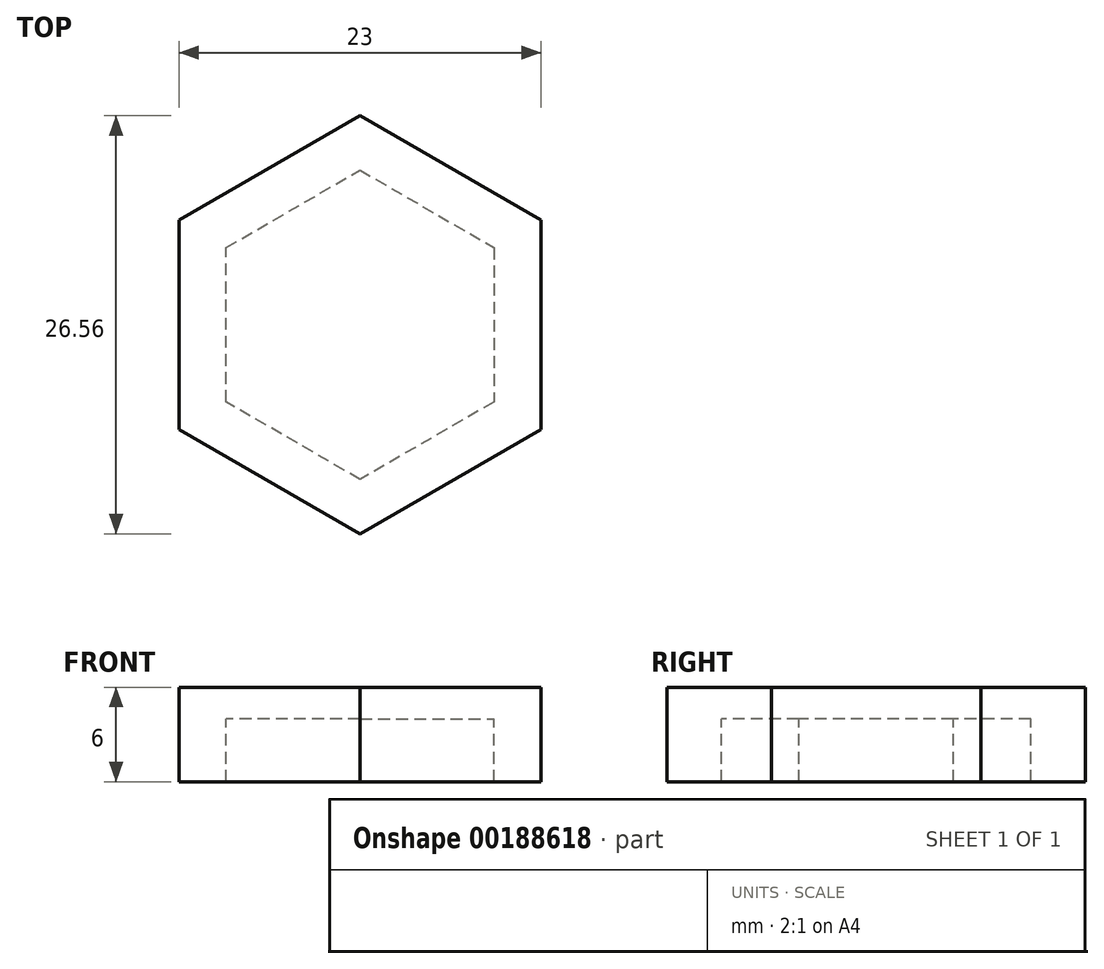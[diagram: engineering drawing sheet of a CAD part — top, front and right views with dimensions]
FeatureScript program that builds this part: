
annotation { "Feature Type Name" : "Feature", "Feature Type Description" : "" }
export const myFeature = defineFeature(function(context is Context, id is Id, definition is map)
    precondition{}
    {
        {
            var Q0;
            Q0=qCreatedBy(makeId("Top.planeOp"),FACE);
            var sketch = newSketch(context, id + "F0", { "sketchPlane" : qUnion([Q0])});
            skCircle(sketch, "E0.cCircle", {"center": v(0, 0) * mm, "radius": 8.5 * mm, "construction": true});
            skLineSegment(sketch, "E0.0", {"start": v(8.5, 4.9) * mm, "end": v(8.5, -4.9) * mm});
            skLineSegment(sketch, "E0.1", {"start": v(8.5, -4.9) * mm, "end": v(0, -9.81) * mm});
            skLineSegment(sketch, "E0.2", {"start": v(0, -9.81) * mm, "end": v(-8.5, -4.9) * mm});
            skLineSegment(sketch, "E0.3", {"start": v(-8.5, -4.9) * mm, "end": v(-8.5, 4.9) * mm});
            skLineSegment(sketch, "E0.4", {"start": v(-8.5, 4.9) * mm, "end": v(0, 9.81) * mm});
            skLineSegment(sketch, "E0.5", {"start": v(0, 9.81) * mm, "end": v(8.5, 4.9) * mm});
            skPoint(sketch, "E0.0.midPoint", {"position": v(8.5, 0) * mm});
            skLineSegment(sketch, "E1.0", {"start": v(0, 13.28) * mm, "end": v(11.5, 6.64) * mm});
            skLineSegment(sketch, "E1.1", {"start": v(11.5, -6.64) * mm, "end": v(0, -13.28) * mm});
            skLineSegment(sketch, "E1.2", {"start": v(0, -13.28) * mm, "end": v(-11.5, -6.64) * mm});
            skLineSegment(sketch, "E1.3", {"start": v(11.5, 6.64) * mm, "end": v(11.5, -6.64) * mm});
            skLineSegment(sketch, "E1.4", {"start": v(-11.5, -6.64) * mm, "end": v(-11.5, 6.64) * mm});
            skLineSegment(sketch, "E1.5", {"start": v(-11.5, 6.64) * mm, "end": v(0, 13.28) * mm});
            skSolve(sketch);
        }
        {
            var Q0;
            Q0=makeQuery(id+"F0.imprint","IMPRINT",FACE,{"disambiguationData":[TD([[makeQuery(id+"F0.imprint","IMPRINT",EDGE,{"derivedFrom":sQuery(id+"F0.wireOp",EDGE,"E0.0")}),1.0]])]});
            extrude(context, id + "F2", {"entities" : qUnion([Q0]), "oppositeDirection" : true, "depth" : 4 * mm});
        }
        {
            var Q0;
            Q0 = qSketchRegion(id + "F0", true);
            var Q1;
            Q1=makeQuery(id+"F0.imprint","IMPRINT",FACE,{"disambiguationData":[TD([[makeQuery(id+"F0.imprint","IMPRINT",EDGE,{"derivedFrom":sQuery(id+"F0.wireOp",EDGE,"E0.0")}),-1.0]])]});
            extrude(context, id + "F1", {"entities" : qUnion([Q0, Q1]), "operationType" : NewBodyOperationType.ADD, "depth" : 2 * mm});
        }
    });
